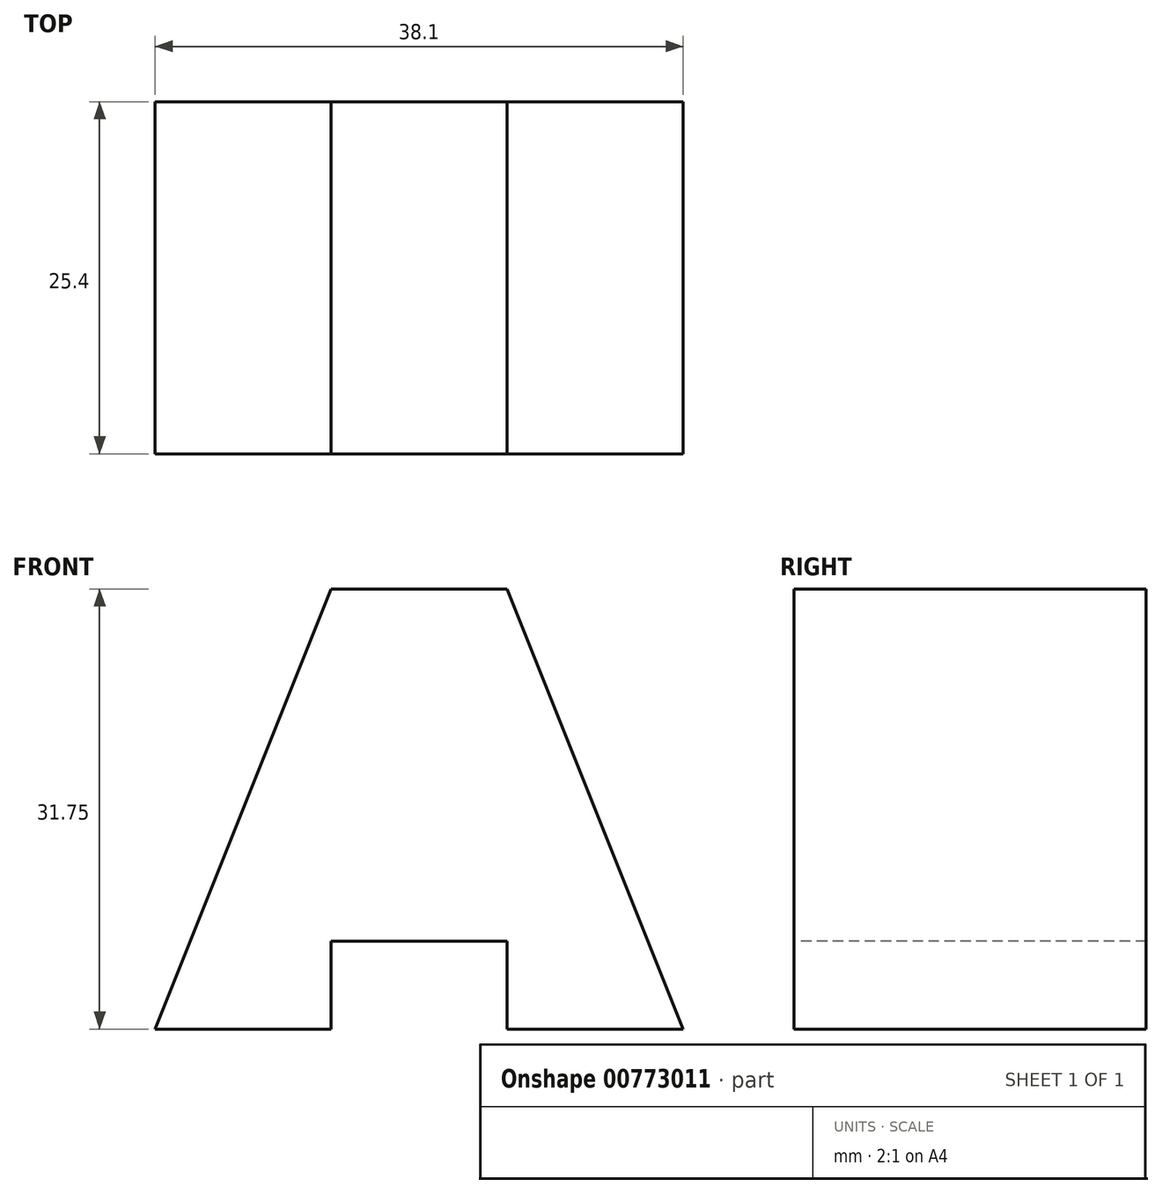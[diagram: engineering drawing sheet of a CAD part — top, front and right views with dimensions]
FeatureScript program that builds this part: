
annotation { "Feature Type Name" : "Feature", "Feature Type Description" : "" }
export const myFeature = defineFeature(function(context is Context, id is Id, definition is map)
    precondition{}
    {
        {
            var Q0;
            Q0=qCreatedBy(makeId("Front.planeOp"),FACE);
            var sketch = newSketch(context, id + "F0", { "sketchPlane" : qUnion([Q0])});
            skLineSegment(sketch, "E0", {"start": v(0, 0) * mm, "end": v(38.1, 0) * mm});
            skLineSegment(sketch, "E1", {"start": v(38.1, 0) * mm, "end": v(38.1, 31.75) * mm});
            skLineSegment(sketch, "E2", {"start": v(38.1, 31.75) * mm, "end": v(0, 31.75) * mm});
            skLineSegment(sketch, "E3", {"start": v(0, 0) * mm, "end": v(0, 31.75) * mm});
            skSolve(sketch);
        }
        {
            var Q0;
            Q0=makeQuery(id+"F0.imprint","IMPRINT",FACE,{"disambiguationData":[TD([[makeQuery(id+"F0.imprint","IMPRINT",EDGE,{"derivedFrom":sQuery(id+"F0.wireOp",EDGE,"E0")}),1.0]])]});
            extrude(context, id + "F1", {"entities" : qUnion([Q0]), "depth" : 25.4 * mm, "offsetDistance" : 25.4 * mm});
        }
        {
            var Q0;
            Q0=makeQuery(id+"F1.opExtrude","CAP_FACE",FACE,{"disambiguationData":[OSD([sQuery(id+"F0.wireOp",EDGE,"E0"),sQuery(id+"F0.wireOp",EDGE,"E1"),sQuery(id+"F0.wireOp",EDGE,"E2"),sQuery(id+"F0.wireOp",EDGE,"E3")])],"isStart":false});
            var sketch = newSketch(context, id + "F2", { "sketchPlane" : qUnion([Q0])});
            skLineSegment(sketch, "E4", {"start": v(0, 0) * mm, "end": v(12.7, 0) * mm});
            skLineSegment(sketch, "E5", {"start": v(12.7, 0) * mm, "end": v(12.7, 6.35) * mm});
            skLineSegment(sketch, "E6", {"start": v(12.7, 6.35) * mm, "end": v(25.4, 6.35) * mm});
            skLineSegment(sketch, "E7", {"start": v(25.4, 6.35) * mm, "end": v(25.4, 0) * mm});
            skLineSegment(sketch, "E8", {"start": v(25.4, 0) * mm, "end": v(38.1, 0) * mm});
            skLineSegment(sketch, "E9", {"start": v(12.7, 6.35) * mm, "end": v(12.7, 31.75) * mm});
            skLineSegment(sketch, "E10", {"start": v(25.4, 6.35) * mm, "end": v(25.4, 31.75) * mm});
            skLineSegment(sketch, "E11", {"start": v(12.7, 31.75) * mm, "end": v(0, 0) * mm});
            skLineSegment(sketch, "E12", {"start": v(25.4, 31.75) * mm, "end": v(38.1, 0) * mm});
            skSolve(sketch);
        }
        {
            var Q0;
            {var subQ0=sQuery(id+"F2.wireOp",EDGE,"E12");Q0=makeQuery(id+"F2.imprint","IMPRINT",FACE,{"disambiguationData":[TD([[makeQuery(id+"F2.imprint","IMPRINT",EDGE,{"derivedFrom":subQ0}),1.0]])]});}
            var Q1;
            {var subQ0=sQuery(id+"F2.wireOp",EDGE,"E11");Q1=makeQuery(id+"F2.imprint","IMPRINT",FACE,{"disambiguationData":[TD([[makeQuery(id+"F2.imprint","IMPRINT",EDGE,{"derivedFrom":subQ0}),-1.0]])]});}
            var Q2;
            {var subQ0=sQuery(id+"F2.wireOp",EDGE,"E5");Q2=makeQuery(id+"F2.imprint","IMPRINT",FACE,{"disambiguationData":[TD([[makeQuery(id+"F2.imprint","IMPRINT",EDGE,{"derivedFrom":subQ0}),-1.0]])]});}
            extrude(context, id + "F3", {"entities" : qUnion([Q0, Q1, Q2]), "operationType" : NewBodyOperationType.REMOVE, "oppositeDirection" : true, "depth" : 25.4 * mm, "offsetDistance" : 25.4 * mm});
        }
    });
